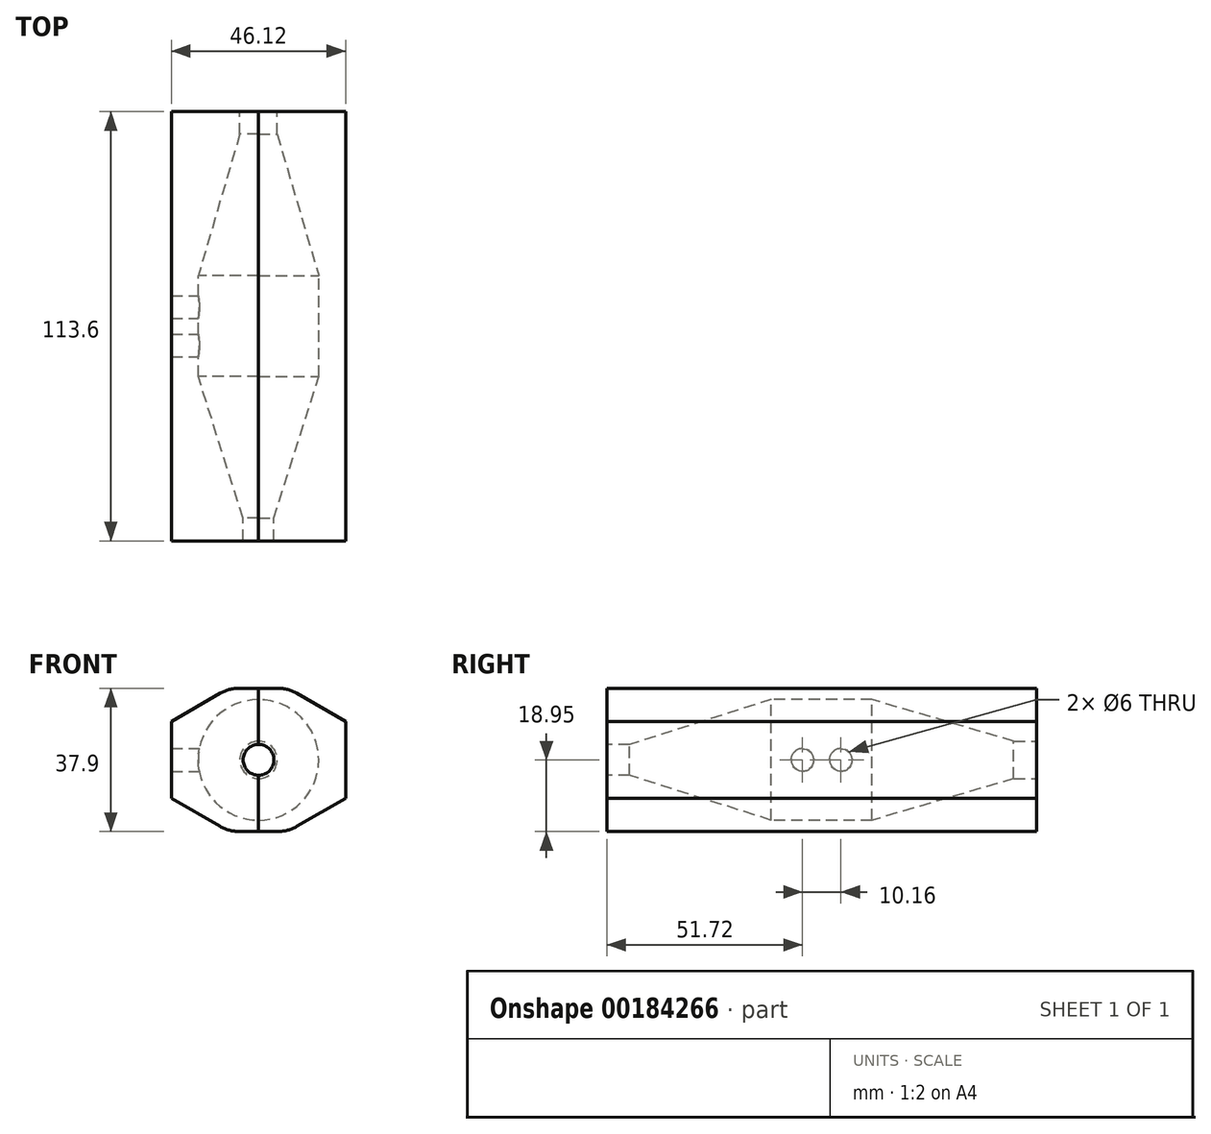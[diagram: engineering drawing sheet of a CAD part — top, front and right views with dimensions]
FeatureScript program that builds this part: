
annotation { "Feature Type Name" : "Feature", "Feature Type Description" : "" }
export const myFeature = defineFeature(function(context is Context, id is Id, definition is map)
    precondition{}
    {
        {
            var Q0;
            Q0=qCreatedBy(makeId("Top.planeOp"),FACE);
            var sketch = newSketch(context, id + "F0", { "sketchPlane" : qUnion([Q0])});
            skLineSegment(sketch, "E0", {"start": v(-4.95, 50.8) * mm, "end": v(-15.95, 13.33) * mm});
            skLineSegment(sketch, "E1", {"start": v(-15.95, 13.33) * mm, "end": v(-15.95, -13.33) * mm});
            skLineSegment(sketch, "E2", {"start": v(-15.95, -13.33) * mm, "end": v(-4.07, -50.8) * mm});
            skLineSegment(sketch, "E3", {"start": v(0, 36.8) * mm, "end": v(0, -34.8) * mm, "construction": true});
            skLineSegment(sketch, "E4", {"start": v(-15.95, 0) * mm, "end": v(0, 0) * mm});
            skLineSegment(sketch, "E5", {"start": v(-18.95, 56.8) * mm, "end": v(-18.95, -56.8) * mm});
            skLineSegment(sketch, "E6", {"start": v(-4.95, 50.8) * mm, "end": v(-4.95, 56.8) * mm});
            skLineSegment(sketch, "E7", {"start": v(-4.95, 56.8) * mm, "end": v(-18.95, 56.8) * mm});
            skLineSegment(sketch, "E8", {"start": v(-4.07, -50.8) * mm, "end": v(-4.07, -56.8) * mm});
            skLineSegment(sketch, "E9", {"start": v(-4.07, -56.8) * mm, "end": v(-18.95, -56.8) * mm});
            skSolve(sketch);
        }
        {
            var Q0;
            Q0 = qSketchRegion(id + "F0", true);
            var Q1;
            Q1=sQuery(id+"F0.wireOp",EDGE,"E3");
            revolve(context, id + "F1", {"entities" : qUnion([Q0]), "axis" : qUnion([Q1]), "revolveType" : RevolveType.SYMMETRIC, "angle" : 180 * degree});
        }
        {
            var Q0;
            Q0=makeQuery(id+"F1.opRevolve","SWEPT_FACE",FACE,{"disambiguationData":[OSD([sQuery(id+"F0.wireOp",EDGE,"E7")])]});
            var sketch = newSketch(context, id + "F2", { "sketchPlane" : qUnion([Q0])});
            skLineSegment(sketch, "E10.bottom", {"start": v(0, 18.95) * mm, "end": v(23.06, 18.95) * mm});
            skLineSegment(sketch, "E10.top", {"start": v(0, -18.95) * mm, "end": v(23.06, -18.95) * mm});
            skLineSegment(sketch, "E10.right", {"start": v(23.06, 18.95) * mm, "end": v(23.06, -18.95) * mm});
            skArc(sketch, "E11.0", {"start": v(0, -18.95) * mm, "mid": v(18.95, 0) * mm, "end": v(0, 18.95) * mm});
            skSolve(sketch);
        }
        {
            var Q0;
            Q0 = qSketchRegion(id + "F2", true);
            var Q1;
            Q1=makeQuery(id+"F1.opRevolve","SWEPT_FACE",FACE,{"disambiguationData":[OSD([sQuery(id+"F0.wireOp",EDGE,"E9")])]});
            extrude(context, id + "F3", {"entities" : qUnion([Q0]), "operationType" : NewBodyOperationType.ADD, "endBound" : BoundingType.UP_TO_SURFACE, "oppositeDirection" : true, "endBoundEntityFace" : qUnion([Q1]), "depth" : 25.4 * mm});
        }
        {
            var Q0;
            Q0=makeQuery(id+"F1.opRevolve","CAP_FACE",FACE,{"disambiguationData":[OSD([sQuery(id+"F0.wireOp",EDGE,"E0"),sQuery(id+"F0.wireOp",EDGE,"E1"),sQuery(id+"F0.wireOp",EDGE,"E2"),sQuery(id+"F0.wireOp",EDGE,"E5"),sQuery(id+"F0.wireOp",EDGE,"E6"),sQuery(id+"F0.wireOp",EDGE,"E7"),sQuery(id+"F0.wireOp",EDGE,"E8"),sQuery(id+"F0.wireOp",EDGE,"E9")])],"isStart":true});
            var sketch = newSketch(context, id + "F4", { "sketchPlane" : qUnion([Q0])});
            skCircle(sketch, "E12", {"center": v(-51.24, 9.88) * mm, "radius": 2.4 * mm});
            skCircle(sketch, "E13", {"center": v(-21.26, 16.34) * mm, "radius": 2.4 * mm});
            skCircle(sketch, "E14", {"center": v(21.06, 16.42) * mm, "radius": 2.4 * mm});
            skCircle(sketch, "E15", {"center": v(50.64, 10.47) * mm, "radius": 2.4 * mm});
            skCircle(sketch, "E16", {"center": v(0, 17.45) * mm, "radius": 2.4 * mm});
            skCircle(sketch, "E17.MirrorC", {"center": v(-21.26, -16.34) * mm, "radius": 2.4 * mm});
            skCircle(sketch, "E18.MirrorC", {"center": v(0, -17.45) * mm, "radius": 2.4 * mm});
            skCircle(sketch, "E19.MirrorC", {"center": v(-51.24, -9.88) * mm, "radius": 2.4 * mm});
            skCircle(sketch, "E20.MirrorC", {"center": v(50.64, -10.47) * mm, "radius": 2.4 * mm});
            skCircle(sketch, "E21.MirrorC", {"center": v(21.06, -16.42) * mm, "radius": 2.4 * mm});
            skLineSegment(sketch, "E22", {"start": v(0, 15.95) * mm, "end": v(0, 18.95) * mm, "construction": true});
            skLineSegment(sketch, "E23", {"start": v(20.32, 13.9) * mm, "end": v(21.8, 18.95) * mm, "construction": true});
            skLineSegment(sketch, "E24", {"start": v(-20.32, 13.74) * mm, "end": v(-22.2, 18.95) * mm, "construction": true});
            skSolve(sketch);
        }
        {
            var Q0;
            Q0=makeQuery(id+"F3.opExtrude","SWEPT_EDGE",EDGE,{"disambiguationData":[OSD([sQuery(id+"F2.wireOp",EDGE,"E10.top"),sQuery(id+"F2.wireOp",EDGE,"E10.right")])]});
            var Q1;
            Q1=makeQuery(id+"F3.opExtrude","SWEPT_EDGE",EDGE,{"disambiguationData":[OSD([sQuery(id+"F2.wireOp",EDGE,"E10.bottom"),sQuery(id+"F2.wireOp",EDGE,"E10.right")])]});
            chamfer(context, id + "F5", {"entities" : qUnion([Q0, Q1]), "chamferType" : ChamferType.OFFSET_ANGLE, "width" : 15.24 * mm, "oppositeDirection" : false, "angle" : 30 * degree, "tangentPropagation" : true});
        }
        {
            var Q0;
            {var subQ0=sQuery(id+"F2.wireOp",EDGE,"E10.bottom");Q0=makeQuery(id+"F5.opChamfer","BLEND_EDGE",EDGE,{"blendedFrom":[makeQuery(id+"F3.opExtrude","SWEPT_EDGE",EDGE,{"disambiguationData":[OSD([subQ0,sQuery(id+"F2.wireOp",EDGE,"E10.right")])]}),makeQuery(id+"F3.opExtrude","SWEPT_FACE",FACE,{"disambiguationData":[OSD([subQ0])]})],"blendedInto":[makeQuery(id+"F3.opExtrude","SWEPT_FACE",FACE,{"disambiguationData":[OSD([subQ0])]})]});}
            var Q1;
            {var subQ0=sQuery(id+"F2.wireOp",EDGE,"E10.top");Q1=makeQuery(id+"F5.opChamfer","BLEND_EDGE",EDGE,{"blendedFrom":[makeQuery(id+"F3.opExtrude","SWEPT_EDGE",EDGE,{"disambiguationData":[OSD([subQ0,sQuery(id+"F2.wireOp",EDGE,"E10.right")])]}),makeQuery(id+"F3.opExtrude","SWEPT_FACE",FACE,{"disambiguationData":[OSD([subQ0])]})],"blendedInto":[makeQuery(id+"F3.opExtrude","SWEPT_FACE",FACE,{"disambiguationData":[OSD([subQ0])]})]});}
            fillet(context, id + "F6", {"entities" : qUnion([Q0, Q1]), "radius" : 10.16 * mm, "tangentPropagation" : true, "allowEdgeOverflow" : false});
        }
        {
            var Q0;
            Q0=makeQuery(id+"F1.opRevolve","CAP_FACE",FACE,{"disambiguationData":[OSD([sQuery(id+"F0.wireOp",EDGE,"E0"),sQuery(id+"F0.wireOp",EDGE,"E1"),sQuery(id+"F0.wireOp",EDGE,"E2"),sQuery(id+"F0.wireOp",EDGE,"E5"),sQuery(id+"F0.wireOp",EDGE,"E6"),sQuery(id+"F0.wireOp",EDGE,"E7"),sQuery(id+"F0.wireOp",EDGE,"E8"),sQuery(id+"F0.wireOp",EDGE,"E9")])],"isStart":true});
            var sketch = newSketch(context, id + "F7", { "sketchPlane" : qUnion([Q0])});
            skCircle(sketch, "E25", {"center": v(-5.08, 0) * mm, "radius": 3 * mm});
            skCircle(sketch, "E26", {"center": v(5.08, 0) * mm, "radius": 3 * mm});
            skSolve(sketch);
        }
        {
            var Q0;
            Q0=makeQuery(id+"F3.opExtrude","SWEPT_FACE",FACE,{"disambiguationData":[OSD([sQuery(id+"F2.wireOp",EDGE,"E10.right")])]});
            var sketch = newSketch(context, id + "F8", { "sketchPlane" : qUnion([Q0])});
            skCircle(sketch, "E27", {"center": v(-22.23, 16.78) * mm, "radius": 3.05 * mm});
            skCircle(sketch, "E28", {"center": v(0, 18.05) * mm, "radius": 3.05 * mm});
            skCircle(sketch, "E29", {"center": v(22.26, 16.7) * mm, "radius": 3.05 * mm});
            skCircle(sketch, "E30", {"center": v(38.6, 7.72) * mm, "radius": 3.05 * mm});
            skCircle(sketch, "E31", {"center": v(-38.6, 9.55) * mm, "radius": 3.05 * mm});
            skCircle(sketch, "E32.MirrorC", {"center": v(22.26, -16.7) * mm, "radius": 3.05 * mm});
            skCircle(sketch, "E33.MirrorC", {"center": v(-38.6, -9.55) * mm, "radius": 3.05 * mm});
            skCircle(sketch, "E34.MirrorC", {"center": v(-22.23, -16.78) * mm, "radius": 3.05 * mm});
            skCircle(sketch, "E35.MirrorC", {"center": v(0, -18.05) * mm, "radius": 3.05 * mm});
            skCircle(sketch, "E36.MirrorC", {"center": v(38.6, -7.72) * mm, "radius": 3.05 * mm});
            skSolve(sketch);
        }
        {
            var Q0;
            Q0=makeQuery(id+"F1.opRevolve","SWEPT_BODY",BODY,{"disambiguationData":[OSD([sQuery(id+"F0.wireOp",EDGE,"E0"),sQuery(id+"F0.wireOp",EDGE,"E1"),sQuery(id+"F0.wireOp",EDGE,"E2"),sQuery(id+"F0.wireOp",EDGE,"E5"),sQuery(id+"F0.wireOp",EDGE,"E6"),sQuery(id+"F0.wireOp",EDGE,"E7"),sQuery(id+"F0.wireOp",EDGE,"E8"),sQuery(id+"F0.wireOp",EDGE,"E9")])]});
            var Q1;
            Q1=qCreatedBy(makeId("Right.planeOp"),FACE);
            mirror(context, id + "F9", {"entities" : qUnion([Q0]), "mirrorPlane" : qUnion([Q1])});
        }
        {
            var Q0;
            Q0 = qSketchRegion(id + "F7", true);
            extrude(context, id + "F10", {"entities" : qUnion([Q0]), "operationType" : NewBodyOperationType.REMOVE, "endBound" : BoundingType.THROUGH_ALL, "oppositeDirection" : true, "depth" : 25.4 * mm, "offsetDistance" : 25.4 * mm});
        }
    });
